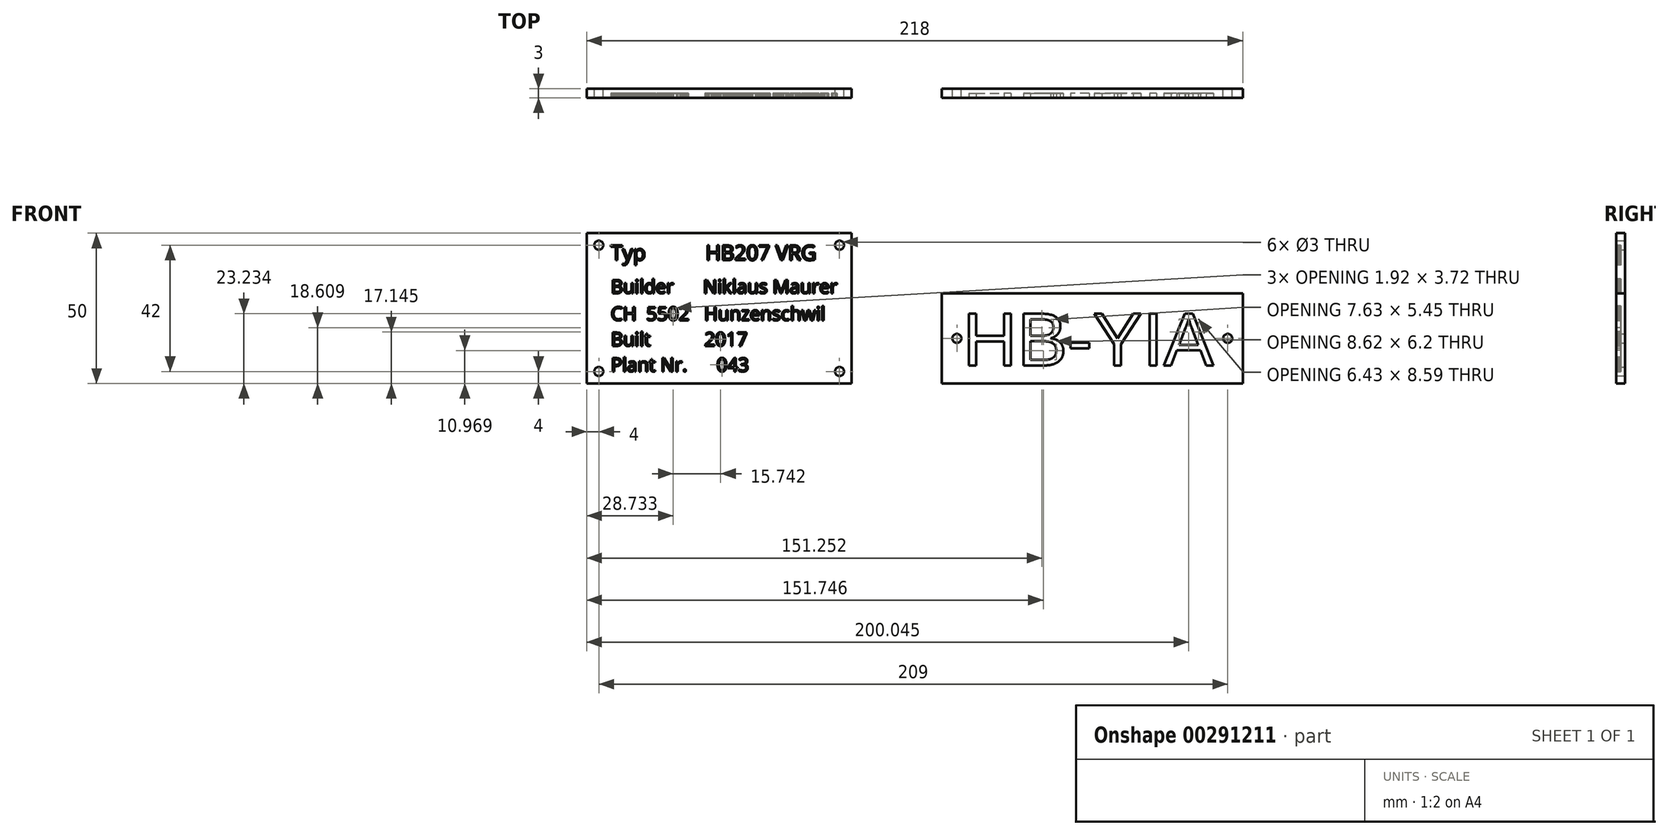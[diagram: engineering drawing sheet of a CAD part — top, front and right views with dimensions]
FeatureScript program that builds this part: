
annotation { "Feature Type Name" : "Feature", "Feature Type Description" : "" }
export const myFeature = defineFeature(function(context is Context, id is Id, definition is map)
    precondition{}
    {
        {
            var Q0;
            Q0=qCreatedBy(makeId("Front.planeOp"),FACE);
            var sketch = newSketch(context, id + "F0", { "sketchPlane" : qUnion([Q0])});
            skLineSegment(sketch, "E0.bottom", {"start": v(0, 0) * mm, "end": v(-88, 0) * mm});
            skLineSegment(sketch, "E0.top", {"start": v(0, 50) * mm, "end": v(-88, 50) * mm});
            skLineSegment(sketch, "E0.left", {"start": v(0, 0) * mm, "end": v(0, 50) * mm});
            skLineSegment(sketch, "E0.right", {"start": v(-88, 0) * mm, "end": v(-88, 50) * mm});
            skLineSegment(sketch, "E1.bottom", {"start": v(30, 0) * mm, "end": v(130, 0) * mm});
            skLineSegment(sketch, "E1.top", {"start": v(30, 30) * mm, "end": v(130, 30) * mm});
            skLineSegment(sketch, "E1.left", {"start": v(30, 0) * mm, "end": v(30, 30) * mm});
            skLineSegment(sketch, "E1.right", {"start": v(130, 0) * mm, "end": v(130, 30) * mm});
            skCircle(sketch, "E2", {"center": v(-4, 4) * mm, "radius": 1.5 * mm});
            skLineSegment(sketch, "E3", {"start": v(-4, 4) * mm, "end": v(-4, 5.5) * mm, "construction": true});
            skLineSegment(sketch, "E4", {"start": v(-4, 4) * mm, "end": v(-4, 46) * mm, "construction": true});
            skLineSegment(sketch, "E5", {"start": v(-4, 4) * mm, "end": v(-84, 4) * mm, "construction": true});
            skLineSegment(sketch, "E6", {"start": v(-84, 4) * mm, "end": v(-84, 46) * mm, "construction": true});
            skLineSegment(sketch, "E7", {"start": v(-4, 46) * mm, "end": v(-84, 46) * mm, "construction": true});
            skCircle(sketch, "E8", {"center": v(-84, 4) * mm, "radius": 1.5 * mm});
            skCircle(sketch, "E9", {"center": v(-4, 46) * mm, "radius": 1.5 * mm});
            skCircle(sketch, "E10", {"center": v(-84, 46) * mm, "radius": 1.5 * mm});
            skCircle(sketch, "E11", {"center": v(35, 15) * mm, "radius": 1.5 * mm});
            skPoint(sketch, "E11.centerSnap0", {"position": v(30, 15) * mm});
            skCircle(sketch, "E12", {"center": v(125, 15) * mm, "radius": 1.5 * mm});
            skPoint(sketch, "E12.centerSnap0", {"position": v(130, 15) * mm});
            skSolve(sketch);
        }
        {
            var Q0;
            Q0=makeQuery(id+"F0.imprint","IMPRINT",FACE,{"disambiguationData":[TD([[makeQuery(id+"F0.imprint","IMPRINT",EDGE,{"derivedFrom":sQuery(id+"F0.wireOp",EDGE,"E0.bottom")}),-1.0]])]});
            var Q1;
            Q1=makeQuery(id+"F0.imprint","IMPRINT",FACE,{"disambiguationData":[TD([[makeQuery(id+"F0.imprint","IMPRINT",EDGE,{"derivedFrom":sQuery(id+"F0.wireOp",EDGE,"E1.bottom")}),1.0]])]});
            extrude(context, id + "F1", {"entities" : qUnion([Q0, Q1]), "depth" : 3 * mm, "offsetDistance" : 25 * mm});
        }
        {
            var Q0;
            Q0=makeQuery(id+"F1.opExtrude","CAP_FACE",FACE,{"disambiguationData":[OSD([sQuery(id+"F0.wireOp",EDGE,"E1.bottom"),sQuery(id+"F0.wireOp",EDGE,"E1.top"),sQuery(id+"F0.wireOp",EDGE,"E1.left"),sQuery(id+"F0.wireOp",EDGE,"E1.right")])],"isStart":false});
            var sketch = newSketch(context, id + "F2", { "sketchPlane" : qUnion([Q0])});
            skText(sketch, "E13", { "text": "HB-YIA", "fontName": "Arimo-Regular.ttf"});
            skText(sketch, "E14", { "text": "Typ           HB207 VRG", "fontName": "OpenSans-Regular.ttf"});
            skText(sketch, "E15", { "text": "Builder      Niklaus Maurer", "fontName": "OpenSans-Regular.ttf"});
            skText(sketch, "E16", { "text": "CH  5502   Hunzenschwil", "fontName": "OpenSans-Regular.ttf"});
            skText(sketch, "E17", { "text": "Built           2017", "fontName": "OpenSans-Regular.ttf"});
            skText(sketch, "E18", { "text": "Plant Nr.      043", "fontName": "OpenSans-Regular.ttf"});
            skPoint(sketch, "E19.endSnap0", {"position": v(-80, 32.25) * mm});
            skLineSegment(sketch, "E20", {"start": v(-80, 46) * mm, "end": v(-80, 4) * mm});
            const initialGuessF2  = {"E13": [0.037, 0.006, 1, 0, 0.018], "E14": [-0.08, 0.041, 1, 0, 0.005], "E15": [-0.08, 0.03, 1, 0, 0.0045], "E16": [-0.08, 0.021, 1, 0, 0.0045], "E17": [-0.08, 0.0125, 1, 0, 0.0045], "E18": [-0.08, 0.004, 1, 0, 0.0045]};
            skSetInitialGuess(sketch, initialGuessF2);
            skSolve(sketch);
        }
        {
            var Q0;
            Q0 = qSketchRegion(id + "F2", true);
            extrude(context, id + "F3", {"entities" : qUnion([Q0]), "oppositeDirection" : true, "depth" : 1.5 * mm, "offsetDistance" : 25 * mm});
        }
    });
